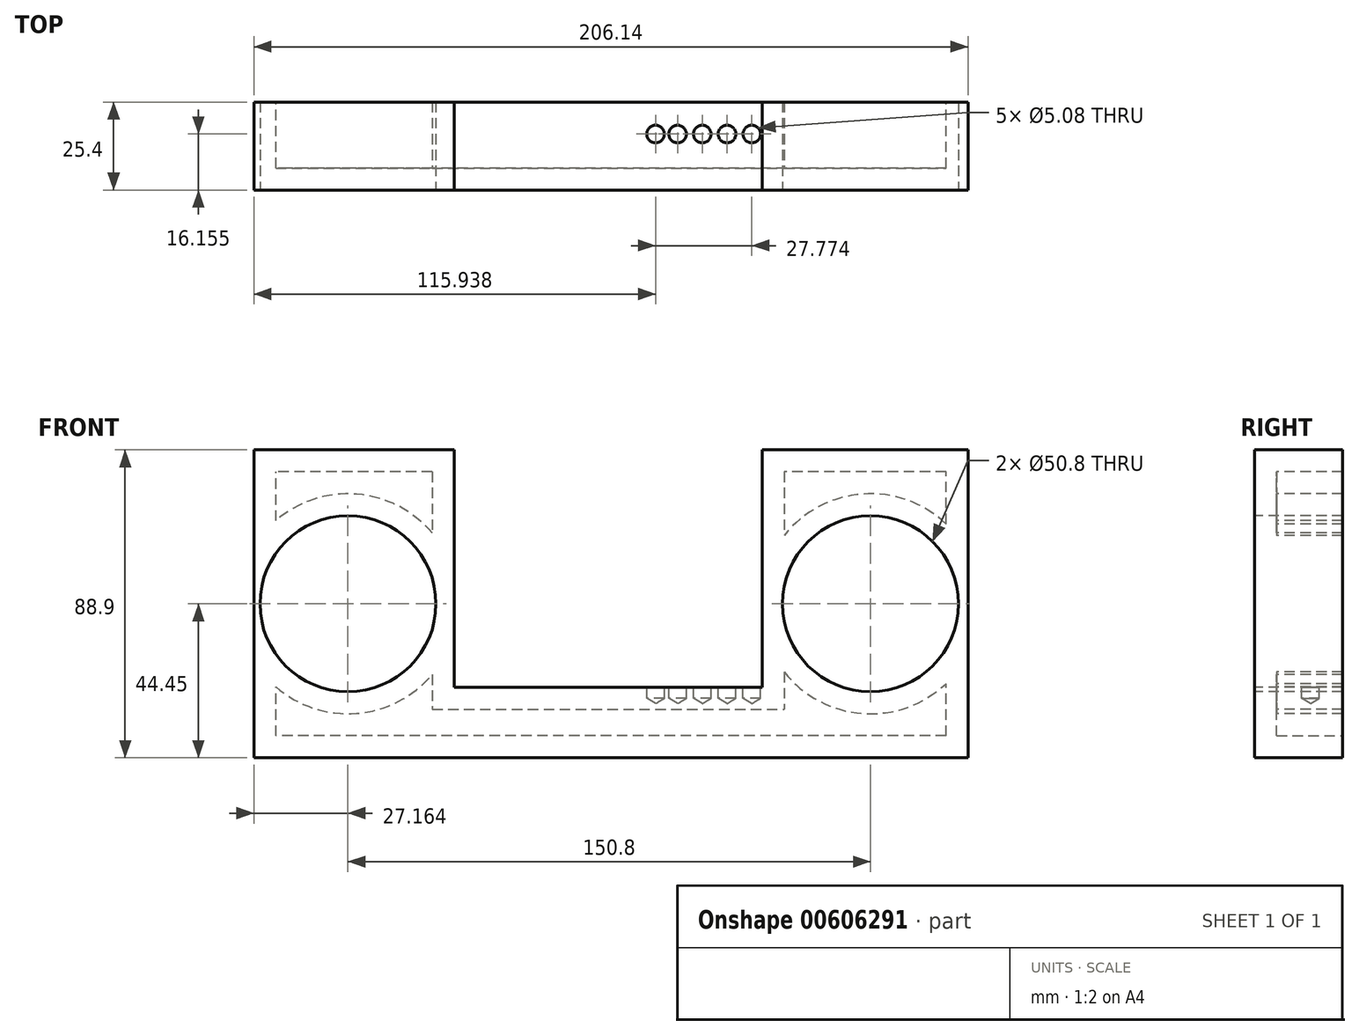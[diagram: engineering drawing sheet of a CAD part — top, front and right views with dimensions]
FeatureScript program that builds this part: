
annotation { "Feature Type Name" : "Feature", "Feature Type Description" : "" }
export const myFeature = defineFeature(function(context is Context, id is Id, definition is map)
    precondition{}
    {
        {
            var Q0;
            Q0=qCreatedBy(makeId("Front.planeOp"),FACE);
            var sketch = newSketch(context, id + "F0", { "sketchPlane" : qUnion([Q0])});
            skLineSegment(sketch, "E0.bottom", {"start": v(103.07, -44.45) * mm, "end": v(-103.07, -44.45) * mm});
            skLineSegment(sketch, "E0.top", {"start": v(103.07, 44.45) * mm, "end": v(-103.07, 44.45) * mm});
            skLineSegment(sketch, "E0.left", {"start": v(103.07, -44.45) * mm, "end": v(103.07, 44.45) * mm});
            skLineSegment(sketch, "E0.right", {"start": v(-103.07, -44.45) * mm, "end": v(-103.07, 44.45) * mm});
            skPoint(sketch, "E0.middle", {"position": v(0, 0) * mm});
            skSolve(sketch);
        }
        {
            var Q0;
            Q0=makeQuery(id+"F0.imprint","IMPRINT",FACE,{"disambiguationData":[TD([[makeQuery(id+"F0.imprint","IMPRINT",EDGE,{"derivedFrom":sQuery(id+"F0.wireOp",EDGE,"E0.bottom")}),-1.0]])]});
            extrude(context, id + "F1", {"entities" : qUnion([Q0]), "depth" : 25.4 * mm, "offsetDistance" : 25.4 * mm});
        }
        {
            var Q0;
            Q0=makeQuery(id+"F1.opExtrude","CAP_FACE",FACE,{"disambiguationData":[OSD([sQuery(id+"F0.wireOp",EDGE,"E0.bottom"),sQuery(id+"F0.wireOp",EDGE,"E0.top"),sQuery(id+"F0.wireOp",EDGE,"E0.left"),sQuery(id+"F0.wireOp",EDGE,"E0.right")])],"isStart":false});
            var sketch = newSketch(context, id + "F2", { "sketchPlane" : qUnion([Q0])});
            skPoint(sketch, "E1", {"position": v(-75.9, 0) * mm});
            skSolve(sketch);
        }
        {
            var Q0;
            Q0=makeQuery(id+"F2.imprint","IMPRINT",FACE,{"disambiguationData":[TD([[makeQuery(id+"F2.imprint","IMPRINT",EDGE,{"derivedFrom":makeQuery(id+"F1.opExtrude","CAP_EDGE",EDGE,{"disambiguationData":[OSD([sQuery(id+"F0.wireOp",EDGE,"E0.bottom")])],"isStart":false})}),-1.0]])]});
            var sketch = newSketch(context, id + "F3", { "sketchPlane" : qUnion([Q0])});
            skPoint(sketch, "E2", {"position": v(74.9, 0) * mm});
            skSolve(sketch);
        }
        {
            var Q0;
            Q0=sQuery(id+"F2.wireOp",VERTEX,"E1");
            var Q1;
            Q1=sQuery(id+"F3.wireOp",VERTEX,"E2");
            var Q2;
            Q2=makeQuery(id+"F1.opExtrude","SWEPT_BODY",BODY,{"disambiguationData":[OSD([sQuery(id+"F0.wireOp",EDGE,"E0.bottom"),sQuery(id+"F0.wireOp",EDGE,"E0.top"),sQuery(id+"F0.wireOp",EDGE,"E0.left"),sQuery(id+"F0.wireOp",EDGE,"E0.right")])]});
            hole(context, id + "F4", {"style" : HoleStyle.SIMPLE, "endStyle" : HoleEndStyle.THROUGH, "holeDiameter" : 50.8 * mm, "majorDiameter" : 6.35 * mm, "isTappedThrough" : true, "tappedDepth" : 12.7 * mm, "tapClearance" : 3, "locations" : qUnion([Q0, Q1]), "scope" : qUnion([Q2])});
        }
        {
            var Q0;
            Q0=makeQuery(id+"F1.opExtrude","CAP_FACE",FACE,{"disambiguationData":[OSD([sQuery(id+"F0.wireOp",EDGE,"E0.bottom"),sQuery(id+"F0.wireOp",EDGE,"E0.top"),sQuery(id+"F0.wireOp",EDGE,"E0.left"),sQuery(id+"F0.wireOp",EDGE,"E0.right")])],"isStart":false});
            var sketch = newSketch(context, id + "F5", { "sketchPlane" : qUnion([Q0])});
            skLineSegment(sketch, "E3.bottom", {"start": v(-45.24, 44.45) * mm, "end": v(43.66, 44.45) * mm});
            skLineSegment(sketch, "E3.top", {"start": v(-45.24, -24.13) * mm, "end": v(43.66, -24.13) * mm});
            skLineSegment(sketch, "E3.left", {"start": v(-45.24, 44.45) * mm, "end": v(-45.24, -24.13) * mm});
            skLineSegment(sketch, "E3.right", {"start": v(43.66, 44.45) * mm, "end": v(43.66, -24.13) * mm});
            skSolve(sketch);
        }
        {
            var Q0;
            Q0 = qSketchRegion(id + "F5", true);
            extrude(context, id + "F6", {"entities" : qUnion([Q0]), "operationType" : NewBodyOperationType.REMOVE, "endBound" : BoundingType.THROUGH_ALL, "oppositeDirection" : true, "depth" : 25.4 * mm, "offsetDistance" : 25.4 * mm});
        }
        {
            var Q0;
            Q0=makeQuery(id+"F1.opExtrude","CAP_FACE",FACE,{"disambiguationData":[OSD([sQuery(id+"F0.wireOp",EDGE,"E0.bottom"),sQuery(id+"F0.wireOp",EDGE,"E0.top"),sQuery(id+"F0.wireOp",EDGE,"E0.left"),sQuery(id+"F0.wireOp",EDGE,"E0.right")])],"isStart":true});
            shell(context, id + "F7", {"entities" : qUnion([Q0]), "thickness" : 6.35 * mm});
        }
        {
            var Q0;
            Q0=makeQuery(id+"F6.boolean.opBoolean","COPY",FACE,{"derivedFrom":makeQuery(id+"F6.opExtrude","SWEPT_FACE",FACE,{"disambiguationData":[OSD([sQuery(id+"F5.wireOp",EDGE,"E3.top")])]})});
            var sketch = newSketch(context, id + "F8", { "sketchPlane" : qUnion([Q0])});
            skPoint(sketch, "E4", {"position": v(40.64, -9.25) * mm});
            skPoint(sketch, "E5", {"position": v(37.33, -9.25) * mm});
            skPoint(sketch, "E6", {"position": v(33.5, -9.25) * mm});
            skPoint(sketch, "E7", {"position": v(29.94, -9.25) * mm});
            skPoint(sketch, "E8", {"position": v(26.37, -9.25) * mm});
            skPoint(sketch, "E9", {"position": v(23.06, -9.25) * mm});
            skPoint(sketch, "E10", {"position": v(19.24, -9.25) * mm});
            skPoint(sketch, "E11", {"position": v(16.18, -9.25) * mm});
            skPoint(sketch, "E12", {"position": v(12.87, -9.25) * mm});
            skPoint(sketch, "E13", {"position": v(9.56, -9.25) * mm});
            skSolve(sketch);
        }
        {
            var Q0;
            Q0=sQuery(id+"F8.wireOp",VERTEX,"E4");
            var Q1;
            Q1=sQuery(id+"F8.wireOp",VERTEX,"E6");
            var Q2;
            Q2=sQuery(id+"F8.wireOp",VERTEX,"E8");
            var Q3;
            Q3=sQuery(id+"F8.wireOp",VERTEX,"E10");
            var Q4;
            Q4=sQuery(id+"F8.wireOp",VERTEX,"E12");
            var Q5;
            Q5=makeQuery(id+"F1.opExtrude","SWEPT_BODY",BODY,{"disambiguationData":[OSD([sQuery(id+"F0.wireOp",EDGE,"E0.bottom"),sQuery(id+"F0.wireOp",EDGE,"E0.top"),sQuery(id+"F0.wireOp",EDGE,"E0.left"),sQuery(id+"F0.wireOp",EDGE,"E0.right")])]});
            hole(context, id + "F9", {"style" : HoleStyle.SIMPLE, "endStyle" : HoleEndStyle.BLIND, "holeDiameter" : 5.08 * mm, "majorDiameter" : 6.35 * mm, "holeDepth" : 3.17 * mm, "isTappedThrough" : true, "tappedDepth" : 12.7 * mm, "tapClearance" : 3, "locations" : qUnion([Q0, Q1, Q2, Q3, Q4]), "scope" : qUnion([Q5])});
        }
    });
